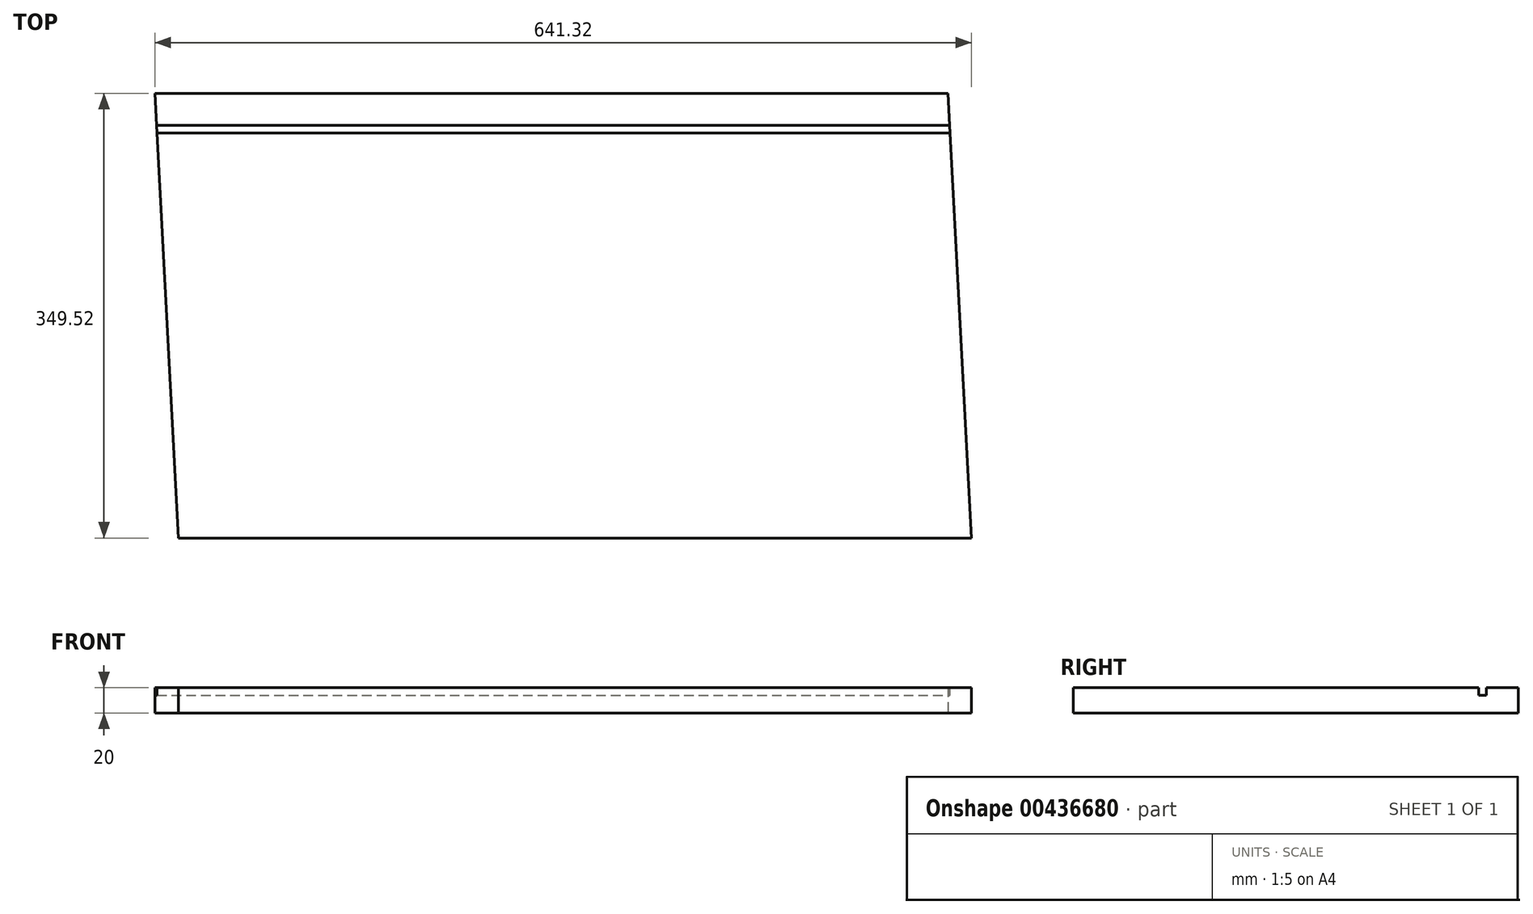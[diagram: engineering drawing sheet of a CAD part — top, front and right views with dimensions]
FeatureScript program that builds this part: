
annotation { "Feature Type Name" : "Feature", "Feature Type Description" : "" }
export const myFeature = defineFeature(function(context is Context, id is Id, definition is map)
    precondition{}
    {
        {
            var Q0;
            Q0=qCreatedBy(makeId("Top.planeOp"),FACE);
            var sketch = newSketch(context, id + "F0", { "sketchPlane" : qUnion([Q0])});
            skLineSegment(sketch, "E0.bottom", {"start": v(320.66, -174.76) * mm, "end": v(-302.34, -174.76) * mm});
            skLineSegment(sketch, "E0.top", {"start": v(302.34, 174.76) * mm, "end": v(-320.66, 174.76) * mm});
            skLineSegment(sketch, "E0.left", {"start": v(320.66, -174.76) * mm, "end": v(302.34, 174.76) * mm});
            skLineSegment(sketch, "E0.right", {"start": v(-302.34, -174.76) * mm, "end": v(-320.66, 174.76) * mm});
            skPoint(sketch, "E0.middle", {"position": v(0, 0) * mm});
            skSolve(sketch);
        }
        {
            var Q0;
            Q0=qSketchRegion(id+"F0",true);
            extrude(context, id + "F1", {"entities" : qUnion([Q0]), "depth" : 20 * mm});
        }
        {
            var Q0;
            Q0=makeQuery(id+"F1.opExtrude","CAP_FACE",FACE,{"disambiguationData":[OSD([sQuery(id+"F0.wireOp",EDGE,"E0.bottom"),sQuery(id+"F0.wireOp",EDGE,"E0.top"),sQuery(id+"F0.wireOp",EDGE,"E0.left"),sQuery(id+"F0.wireOp",EDGE,"E0.right")])],"isStart":false});
            var sketch = newSketch(context, id + "F2", { "sketchPlane" : qUnion([Q0])});
            skLineSegment(sketch, "E1.bottom", {"start": v(-319.35, 149.76) * mm, "end": v(303.97, 149.76) * mm});
            skLineSegment(sketch, "E1.top", {"start": v(-319.35, 143.76) * mm, "end": v(303.97, 143.76) * mm});
            skLineSegment(sketch, "E1.left", {"start": v(-319.35, 149.76) * mm, "end": v(-319.35, 143.76) * mm});
            skLineSegment(sketch, "E1.right", {"start": v(303.97, 149.76) * mm, "end": v(303.97, 143.76) * mm});
            skSolve(sketch);
        }
        {
            var Q0;
            Q0=qSketchRegion(id+"F2",true);
            extrude(context, id + "F3", {"entities" : qUnion([Q0]), "operationType" : NewBodyOperationType.REMOVE, "oppositeDirection" : true, "depth" : 6 * mm});
        }
    });
